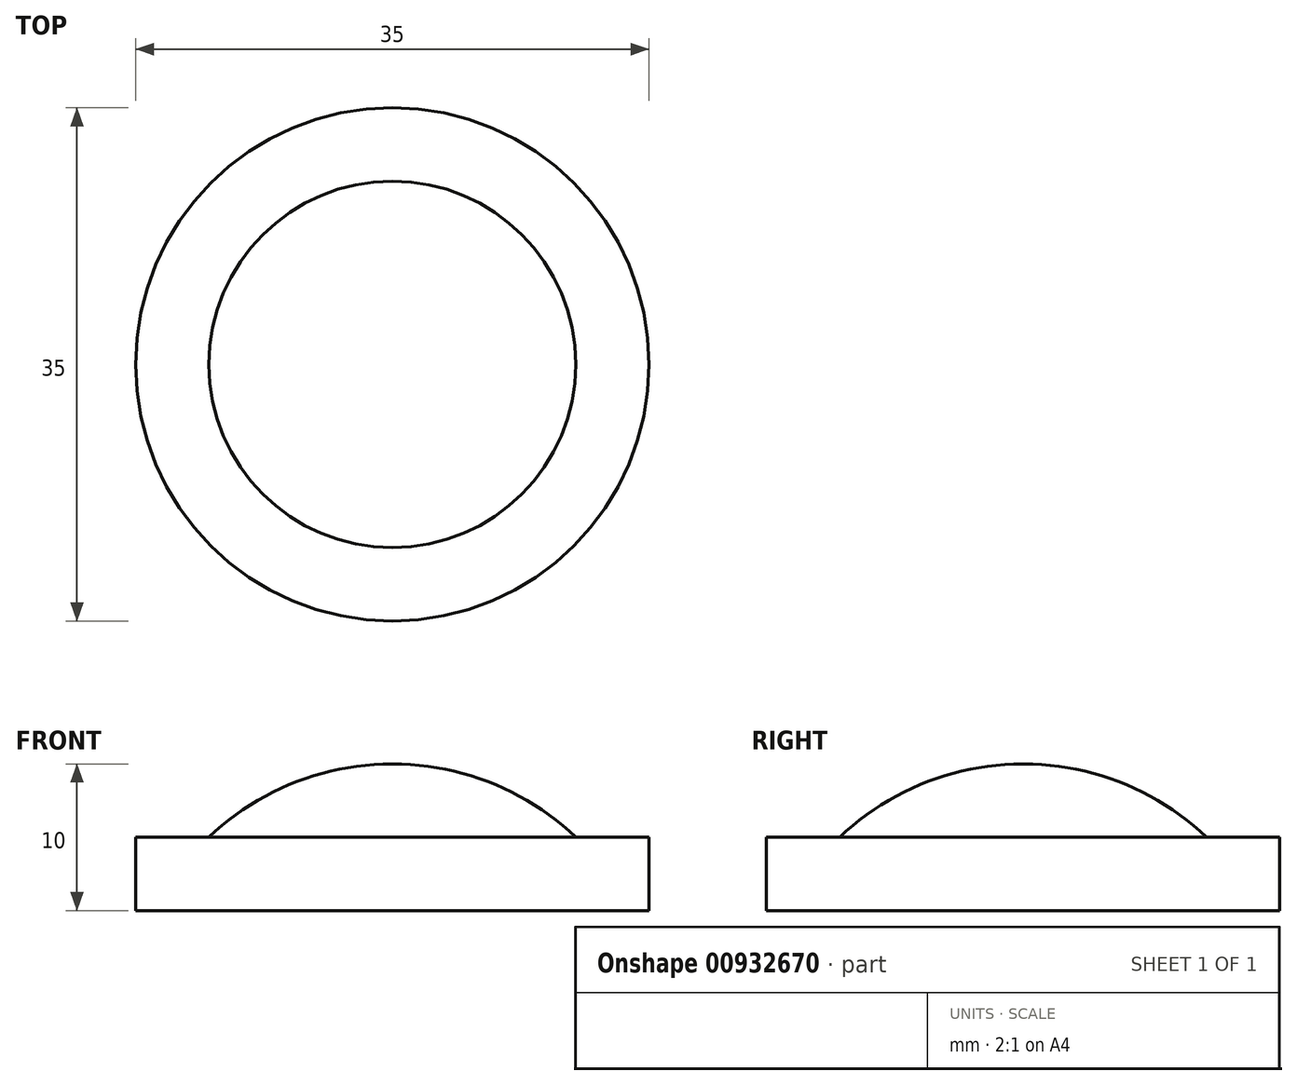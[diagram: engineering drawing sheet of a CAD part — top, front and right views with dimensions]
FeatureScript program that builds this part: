
annotation { "Feature Type Name" : "Feature", "Feature Type Description" : "" }
export const myFeature = defineFeature(function(context is Context, id is Id, definition is map)
    precondition{}
    {
        {
            var Q0;
            Q0=qCreatedBy(makeId("Top.planeOp"),FACE);
            var sketch = newSketch(context, id + "F0", { "sketchPlane" : qUnion([Q0])});
            skCircle(sketch, "E0", {"center": v(0, 0) * mm, "radius": 17.5 * mm});
            skSolve(sketch);
        }
        {
            var Q0;
            Q0=makeQuery(id+"F0.imprint","IMPRINT",FACE,{"disambiguationData":[TD([[makeQuery(id+"F0.imprint","IMPRINT",EDGE,{"derivedFrom":sQuery(id+"F0.wireOp",EDGE,"E0")}),1.0]])]});
            extrude(context, id + "F1", {"entities" : qUnion([Q0]), "depth" : 5 * mm, "offsetDistance" : 25 * mm});
        }
        {
            var Q0;
            Q0=makeQuery(id+"F1.opExtrude","CAP_FACE",FACE,{"disambiguationData":[OSD([sQuery(id+"F0.wireOp",EDGE,"E0")])],"isStart":false});
            var sketch = newSketch(context, id + "F2", { "sketchPlane" : qUnion([Q0])});
            skCircle(sketch, "E1", {"center": v(0, 0) * mm, "radius": 12.5 * mm});
            skSolve(sketch);
        }
        {
            var Q0;
            Q0=makeQuery(id+"F2.imprint","IMPRINT",FACE,{"disambiguationData":[TD([[makeQuery(id+"F2.imprint","IMPRINT",EDGE,{"derivedFrom":sQuery(id+"F2.wireOp",EDGE,"E1")}),1.0]])]});
            extrude(context, id + "F3", {"entities" : qUnion([Q0]), "operationType" : NewBodyOperationType.ADD, "depth" : 5 * mm, "offsetDistance" : 25 * mm});
        }
        {
            var Q0;
            Q0=makeQuery(id+"F3.opExtrude","CAP_EDGE",EDGE,{"disambiguationData":[OSD([sQuery(id+"F2.wireOp",EDGE,"E1")])],"isStart":false});
            fillet(context, id + "F4", {"entities" : qUnion([Q0]), "tangentPropagation" : true, "radius" : 18 * mm, "defaultsChanged" : true, "vertexSettings" : [], "allowEdgeOverflow" : false});
        }
    });
